# Revit family: Hekatron_Raumlufttechnik_LRS 01_DE_22.01
name_source: partatom
category: Brandmelder
revit_build: Autodesk Revit 2018 (Build: 20190510_1515(x64)
units: mm (PartAtom-declared; Revit-internal decimal feet)

## family parameters
Basisbauteil = Fläche
Beim Laden mit Abzugskörper schneiden = Nein
Bemaßung runder Anschluss = Durchmesser verwenden
Beschriftungsausrichtung beibehalten = Ja
Gemeinsam genutzt = Nein
OmniClass-Nummer = 23.85.30.21
OmniClass-Titel = Environmental Detection/Registration
Raumberechnungspunkt = Nein
Teiletyp = Normal

## types (1)
- LRS 01
    Beschreibung = Lüftungs-Rauchschalter-System zur Rauchüberwachung von Lüftungsleitungen, Steuerungen von Lüftungsanlagen und weiteren Anwendungen.
    Betriebsspannung = 18 bis 28 V DC
    Breite (mm) = 247.0
    Farbe = blau
    Funktionsprinzip = optisch
    Hersteller = Hekatron
    Höhe (mm) = 441.0
    Kabeleinführung = seitlich
    Link zu Ausschreibungstext = https://www.meinhplus.de
    Link zu Produktinformation = https://www.hekatron-planungstools.de
    Link zu ausschreiben.de = http://www.ausschreiben.de
    Link zum Datenblatt = https://www.hekatron-planungstools.de
    Material = PC / eloxiertes Alurohr
    Modell = LRS 01
    Montageart = am Kanal
    Nettogewicht (g) = 120.0
    Schutzart = IP 54
    Stromaufnahme = max. 22mA
    Tiefe (mm) = 135.0
    Typenkommentare = Lüftungsrauchschalter System LRS 01, 24V, DC, VdS
    UB A&S Artikel Nummer = 5000605-0201
    URL = https://www.hekatron-brandschutz.de
    VdS-Anerkennung = G 207083
    Version des BIM Objektes = 22.01
    Vorgabe-Ansicht = 1200 mm
    Zulässige Luftgeschwindigkeit = 1 bis 20 m/s
    Zulässige Umgebungstemperatur = -20 °C bis +60 °C

## geometry (parser evidence)
native form markers: Sweep x3
no freeform markers — native parametric forms only
